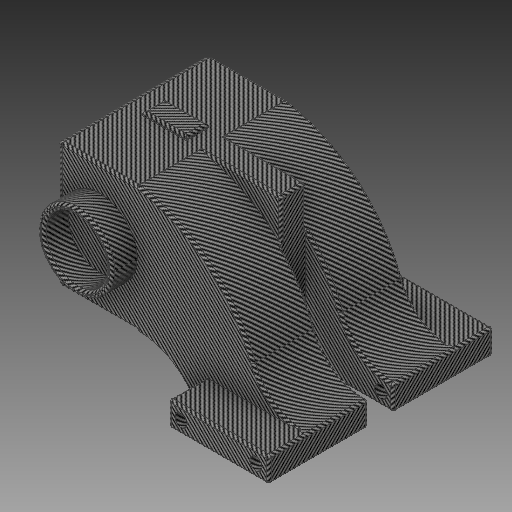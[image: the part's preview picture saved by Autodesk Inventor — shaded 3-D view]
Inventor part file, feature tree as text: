
AUTODESK INVENTOR PART (.ipt)
format: ipt  version: 2018 (Build 220112000, 112)  size: 557,056 bytes
history: native  units: mm
features: sketch x9, fillet x8, extrude x7, mirror x3
ambient origin geometry x8: Origin, YZ Plane, XZ Plane, XY Plane, X Axis, Y Axis, Z Axis, Center Point
bodies: Solid1 (feature_tree)
feature tree (27):
  extrude  "Extrusion1"  Depth=50.0mm TaperAngle=0.0deg
  sketch  "Sketch2"  dims[d6=30.0mm d7=0.0mm d10=3.0mm d11=0.0mm]
  extrude  "Extrusion2"  Depth=3.0mm TaperAngle=0.0deg
  sketch  "Sketch4"  dims[d24=180.1mm d25=0.0mm d26=5.0mm]
  mirror  "Mirror1"
  extrude  "Extrusion3"  Depth=180.1mm TaperAngle=0.0deg
  mirror  "Mirror2"
  extrude  "Extrusion4"  Depth=5.0mm
  extrude  "Extrusion5"  Depth=2.0mm
  mirror  "Mirror3"
  extrude  "Extrusion6"  Depth=2.0mm
  extrude  "Extrusion7"  Depth=2.0mm
  fillet  "Fillet1"  Radius=2.0mm
  fillet  "Fillet2"  [1 undecoded]
  fillet  "Fillet3"  [1 undecoded]
  fillet  "Fillet4"  [1 undecoded]
  fillet  "Fillet5"  [1 undecoded]
  fillet  "Fillet6"  [1 undecoded]
  fillet  "Fillet7"  [1 undecoded]
  fillet  "Fillet8"  [1 undecoded]
  sketch  "Sketch1"  dims[d2=20.0mm d3=0.0mm d4=50.0mm d5=0.0mm]
  sketch  "Sketch3"  dims[d14=20.0mm d15=0.0mm d20=180.1mm d21=0.0mm]
  sketch  "Sketch5"  dims[d27=2.0mm d28=2.0mm]
  sketch  "Sketch6"  dims[d29=2.0mm d30=2.0mm]
  sketch  "Sketch7"  dims[d31=2.0mm d32=2.0mm d33=2.0mm]
  sketch  "Sketch8"
  sketch  "Sketch9"
note: 7 required parameter values undecoded (feature->parameter linkage not recoverable at this tier; creation-order binding heuristic only, values carry confidence <= 0.55)
